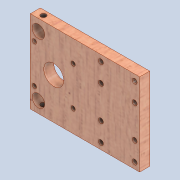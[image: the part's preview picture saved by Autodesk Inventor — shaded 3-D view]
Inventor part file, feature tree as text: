
AUTODESK INVENTOR PART (.ipt)
format: ipt  version: 2020 (Build 240168000, 168)  size: 208,384 bytes
history: native  units: mm
features: sketch x6, other x6, extrude x4, reference x4, hole x3, pattern_linear x2
ambient origin geometry x8: Origin, YZ Plane, XZ Plane, XY Plane, X Axis, Y Axis, Z Axis, Center Point
bodies: Solid1 (feature_tree)
feature tree (25):
  extrude  "Extrusion1"  Depth=66.0mm
  extrude  "Extrusion4"  TaperAngle=0.0deg  [1 undecoded]
  extrude  "Extrusion5"  TaperAngle=0.0deg  [1 undecoded]
  extrude  "Extrusion6"  Depth=9.0mm
  hole  "Hole1"  [1 undecoded]
  pattern_linear  "Rectangular Pattern1"  Spacing1=18.748842mm  [1 undecoded]
  pattern_linear  "Rectangular Pattern2"  Spacing1=3.5mm  [1 undecoded]
  hole  "Hole2"  [1 undecoded]
  hole  "Hole3"  [1 undecoded]
  sketch  "Sketch1"  dims[d0=87.5mm d1=66.0mm]
  sketch  "Sketch4"  dims[d2=8.0mm d3=0.0mm d19=0.0mm d20=0.0mm]
  sketch  "Sketch6"  dims[d24=16.0mm d25=0.0mm d26=0.0mm]
  reference  "Reference7"
  reference  "Reference8"
  sketch  "Sketch8"  dims[d27=6.5mm d28=9.0mm]
  reference  "Reference9"
  reference  "Reference10"
  sketch  "Sketch9"  dims[d29=10.0mm d30=9.0mm]
  sketch  "Sketch10"  dims[d31=0.0mm d32=0.0mm d33=18.748842mm d35=3.5mm d36=31.0mm d38=5.0mm d39=15.0mm d40=26.0mm d41=15.0mm d42=4.0mm d43=4.0mm d44=6.0mm d45=4.0mm d46=2.0mm d47=90.0deg d48=8.0mm d49=20.594885mm d50=20.0mm d52=15.0mm d53=20.0mm d55=41.0mm d56=20.0mm d58=27.0mm d59=6.5mm d60=4.134mm d61=5.0mm d62=4.0mm d63=2.0mm d64=90.0deg d65=7.45mm d66=20.594885mm d67=4.134mm d68=5.0mm d69=4.0mm d70=2.0mm d71=90.0deg d72=7.45mm d73=20.594885mm]
  parser-record x1  (decoder bookkeeping rows leaked as tree rows — omitted from the tree; the rows remain in map.json)
  other  "0005-00-00 Ansamblu_General.iam"
  other  "0005-10-1001 NEMA17 - Motor de passo.ipt:23"
  other  "0005-10-04 Z axis and extruder.iam"
  other  "0005-10-10-1003 LeadScrew 8mm x 2mmPitch.ipt:21"
  other  "0005-10-1002  Hub.ipt:22"
note: 7 required parameter values undecoded (feature->parameter linkage not recoverable at this tier; creation-order binding heuristic only, values carry confidence <= 0.55)
note: 1 file-system path scrubbed to <path> (originals preserved in map.json)
